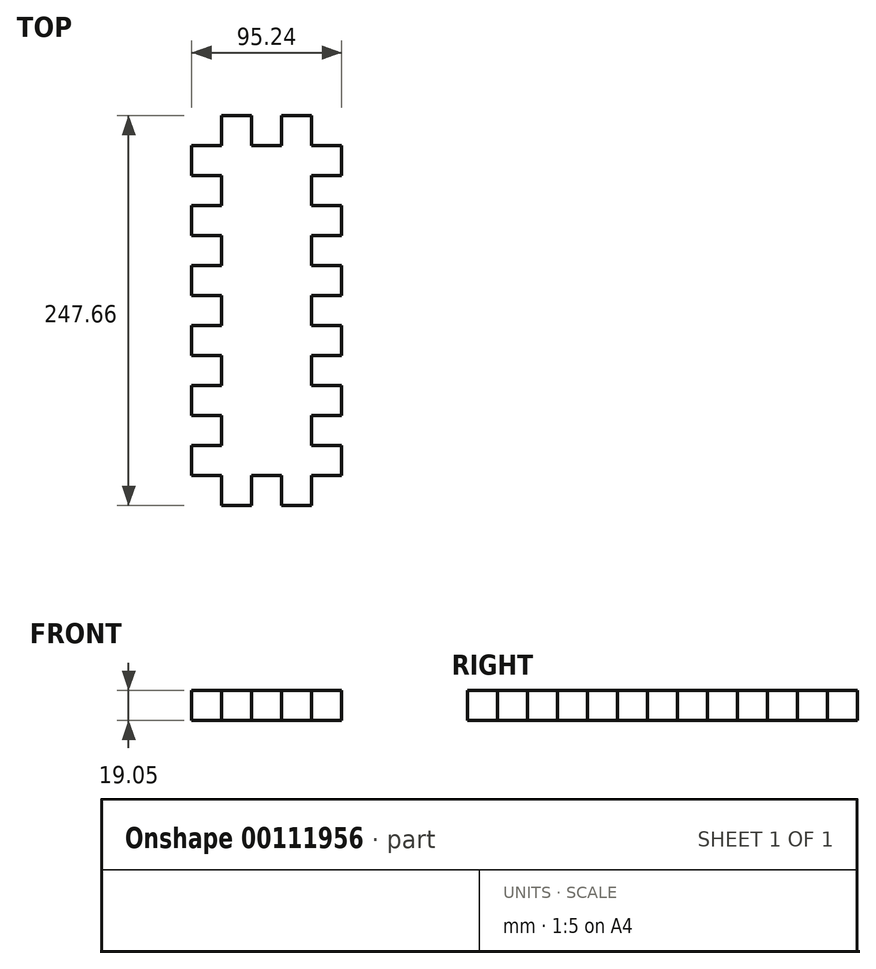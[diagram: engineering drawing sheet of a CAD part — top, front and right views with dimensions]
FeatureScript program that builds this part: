
annotation { "Feature Type Name" : "Feature", "Feature Type Description" : "" }
export const myFeature = defineFeature(function(context is Context, id is Id, definition is map)
    precondition{}
    {
        {
            var Q0;
            Q0=qCreatedBy(makeId("Top.planeOp"),FACE);
            var sketch = newSketch(context, id + "F0", { "sketchPlane" : qUnion([Q0])});
            skLineSegment(sketch, "E0.bottom", {"start": v(-47.62, 123.83) * mm, "end": v(47.63, 123.83) * mm});
            skLineSegment(sketch, "E0.top", {"start": v(-47.63, -123.83) * mm, "end": v(47.62, -123.83) * mm});
            skLineSegment(sketch, "E0.left", {"start": v(-47.62, 123.83) * mm, "end": v(-47.63, -123.83) * mm});
            skLineSegment(sketch, "E0.right", {"start": v(47.63, 123.83) * mm, "end": v(47.62, -123.83) * mm});
            skPoint(sketch, "E0.middle", {"position": v(0, 0) * mm});
            skSolve(sketch);
        }
        {
            var Q0;
            Q0 = qSketchRegion(id + "F0", true);
            extrude(context, id + "F1", {"entities" : qUnion([Q0]), "depth" : 19.05 * mm});
        }
        {
            var Q0;
            Q0=makeQuery(id+"F1.opExtrude","CAP_FACE",FACE,{"disambiguationData":[OSD([sQuery(id+"F0.wireOp",EDGE,"E0.bottom"),sQuery(id+"F0.wireOp",EDGE,"E0.top"),sQuery(id+"F0.wireOp",EDGE,"E0.left"),sQuery(id+"F0.wireOp",EDGE,"E0.right")])],"isStart":false});
            var sketch = newSketch(context, id + "F2", { "sketchPlane" : qUnion([Q0])});
            skLineSegment(sketch, "E1.bottom", {"start": v(-47.62, 123.83) * mm, "end": v(-28.57, 123.83) * mm});
            skLineSegment(sketch, "E1.top", {"start": v(-47.62, 104.78) * mm, "end": v(-28.57, 104.78) * mm});
            skLineSegment(sketch, "E1.left", {"start": v(-47.62, 123.83) * mm, "end": v(-47.62, 104.78) * mm});
            skLineSegment(sketch, "E1.right", {"start": v(-28.57, 123.83) * mm, "end": v(-28.57, 104.78) * mm});
            skLineSegment(sketch, "E2.1.0.0", {"start": v(9.53, 123.83) * mm, "end": v(9.53, 104.78) * mm});
            skLineSegment(sketch, "E2.1.0.1", {"start": v(-9.52, 123.83) * mm, "end": v(-9.52, 104.78) * mm});
            skLineSegment(sketch, "E2.1.0.2", {"start": v(-9.52, 104.78) * mm, "end": v(9.53, 104.78) * mm});
            skLineSegment(sketch, "E2.1.0.3", {"start": v(-9.52, 123.83) * mm, "end": v(9.53, 123.83) * mm});
            skLineSegment(sketch, "E2.2.0.0", {"start": v(47.63, 123.83) * mm, "end": v(47.63, 104.78) * mm});
            skLineSegment(sketch, "E2.2.0.1", {"start": v(28.58, 123.83) * mm, "end": v(28.58, 104.78) * mm});
            skLineSegment(sketch, "E2.2.0.2", {"start": v(28.58, 104.78) * mm, "end": v(47.63, 104.78) * mm});
            skLineSegment(sketch, "E2.2.0.3", {"start": v(28.58, 123.83) * mm, "end": v(47.63, 123.83) * mm});
            skLineSegment(sketch, "E2.direction1", {"start": v(-47.62, 104.78) * mm, "end": v(-9.52, 104.78) * mm, "construction": true});
            skLineSegment(sketch, "E3.0.1.0", {"start": v(-47.62, 85.73) * mm, "end": v(-28.57, 85.73) * mm});
            skLineSegment(sketch, "E3.0.1.1", {"start": v(-47.62, 66.68) * mm, "end": v(-28.57, 66.68) * mm});
            skLineSegment(sketch, "E3.0.1.2", {"start": v(-47.62, 85.73) * mm, "end": v(-47.62, 66.68) * mm});
            skLineSegment(sketch, "E3.0.1.3", {"start": v(-28.57, 85.73) * mm, "end": v(-28.57, 66.68) * mm});
            skLineSegment(sketch, "E3.0.2.0", {"start": v(-47.62, 47.63) * mm, "end": v(-28.57, 47.63) * mm});
            skLineSegment(sketch, "E3.0.2.1", {"start": v(-47.62, 28.58) * mm, "end": v(-28.57, 28.58) * mm});
            skLineSegment(sketch, "E3.0.2.2", {"start": v(-47.62, 47.63) * mm, "end": v(-47.62, 28.58) * mm});
            skLineSegment(sketch, "E3.0.2.3", {"start": v(-28.57, 47.63) * mm, "end": v(-28.57, 28.58) * mm});
            skLineSegment(sketch, "E3.0.3.0", {"start": v(-47.62, 9.53) * mm, "end": v(-28.57, 9.53) * mm});
            skLineSegment(sketch, "E3.0.3.1", {"start": v(-47.62, -9.52) * mm, "end": v(-28.57, -9.52) * mm});
            skLineSegment(sketch, "E3.0.3.2", {"start": v(-47.62, 9.53) * mm, "end": v(-47.62, -9.52) * mm});
            skLineSegment(sketch, "E3.0.3.3", {"start": v(-28.57, 9.53) * mm, "end": v(-28.57, -9.52) * mm});
            skLineSegment(sketch, "E3.0.4.0", {"start": v(-47.62, -28.57) * mm, "end": v(-28.57, -28.57) * mm});
            skLineSegment(sketch, "E3.0.4.1", {"start": v(-47.62, -47.62) * mm, "end": v(-28.57, -47.62) * mm});
            skLineSegment(sketch, "E3.0.4.2", {"start": v(-47.62, -28.57) * mm, "end": v(-47.62, -47.62) * mm});
            skLineSegment(sketch, "E3.0.4.3", {"start": v(-28.57, -28.57) * mm, "end": v(-28.57, -47.62) * mm});
            skLineSegment(sketch, "E3.0.5.0", {"start": v(-47.62, -66.67) * mm, "end": v(-28.57, -66.67) * mm});
            skLineSegment(sketch, "E3.0.5.1", {"start": v(-47.62, -85.72) * mm, "end": v(-28.57, -85.72) * mm});
            skLineSegment(sketch, "E3.0.5.2", {"start": v(-47.62, -66.67) * mm, "end": v(-47.62, -85.72) * mm});
            skLineSegment(sketch, "E3.0.5.3", {"start": v(-28.57, -66.67) * mm, "end": v(-28.57, -85.72) * mm});
            skLineSegment(sketch, "E3.direction1", {"start": v(-47.62, 104.78) * mm, "end": v(-22.22, 104.78) * mm, "construction": true});
            skLineSegment(sketch, "E3.direction2", {"start": v(-47.62, 104.78) * mm, "end": v(-47.62, 66.68) * mm, "construction": true});
            skLineSegment(sketch, "E4.0.0.6", {"start": v(-47.62, -104.77) * mm, "end": v(-28.57, -104.77) * mm});
            skLineSegment(sketch, "E4.3.0.6", {"start": v(-47.62, -123.82) * mm, "end": v(-28.57, -123.82) * mm});
            skLineSegment(sketch, "E4.6.0.6", {"start": v(-47.62, -104.77) * mm, "end": v(-47.62, -123.82) * mm});
            skLineSegment(sketch, "E4.9.0.6", {"start": v(-28.57, -104.77) * mm, "end": v(-28.57, -123.82) * mm});
            skLineSegment(sketch, "E5.1.0.0", {"start": v(-9.52, -104.77) * mm, "end": v(9.53, -104.77) * mm});
            skLineSegment(sketch, "E5.1.0.1", {"start": v(-9.52, -123.82) * mm, "end": v(9.53, -123.82) * mm});
            skLineSegment(sketch, "E5.1.0.2", {"start": v(-9.52, -104.77) * mm, "end": v(-9.52, -123.82) * mm});
            skLineSegment(sketch, "E5.1.0.3", {"start": v(9.53, -104.77) * mm, "end": v(9.53, -123.82) * mm});
            skLineSegment(sketch, "E5.2.0.0", {"start": v(28.58, -104.77) * mm, "end": v(47.63, -104.77) * mm});
            skLineSegment(sketch, "E5.2.0.1", {"start": v(28.58, -123.82) * mm, "end": v(47.63, -123.82) * mm});
            skLineSegment(sketch, "E5.2.0.2", {"start": v(28.58, -104.77) * mm, "end": v(28.58, -123.82) * mm});
            skLineSegment(sketch, "E5.2.0.3", {"start": v(47.63, -104.77) * mm, "end": v(47.63, -123.82) * mm});
            skLineSegment(sketch, "E5.direction1", {"start": v(-47.62, -123.82) * mm, "end": v(-9.52, -123.82) * mm, "construction": true});
            skLineSegment(sketch, "E6.0.1.0", {"start": v(28.58, -66.67) * mm, "end": v(47.63, -66.67) * mm});
            skLineSegment(sketch, "E6.0.1.1", {"start": v(28.58, -66.67) * mm, "end": v(28.58, -85.72) * mm});
            skLineSegment(sketch, "E6.0.1.2", {"start": v(47.63, -66.67) * mm, "end": v(47.63, -85.72) * mm});
            skLineSegment(sketch, "E6.0.1.3", {"start": v(28.58, -85.72) * mm, "end": v(47.63, -85.72) * mm});
            skLineSegment(sketch, "E6.0.2.0", {"start": v(28.58, -28.57) * mm, "end": v(47.63, -28.57) * mm});
            skLineSegment(sketch, "E6.0.2.1", {"start": v(28.58, -28.57) * mm, "end": v(28.58, -47.62) * mm});
            skLineSegment(sketch, "E6.0.2.2", {"start": v(47.63, -28.57) * mm, "end": v(47.63, -47.62) * mm});
            skLineSegment(sketch, "E6.0.2.3", {"start": v(28.58, -47.62) * mm, "end": v(47.63, -47.62) * mm});
            skLineSegment(sketch, "E6.0.3.0", {"start": v(28.58, 9.53) * mm, "end": v(47.63, 9.53) * mm});
            skLineSegment(sketch, "E6.0.3.1", {"start": v(28.58, 9.53) * mm, "end": v(28.58, -9.52) * mm});
            skLineSegment(sketch, "E6.0.3.2", {"start": v(47.63, 9.53) * mm, "end": v(47.63, -9.52) * mm});
            skLineSegment(sketch, "E6.0.3.3", {"start": v(28.58, -9.52) * mm, "end": v(47.63, -9.52) * mm});
            skLineSegment(sketch, "E6.0.4.0", {"start": v(28.58, 47.63) * mm, "end": v(47.63, 47.63) * mm});
            skLineSegment(sketch, "E6.0.4.1", {"start": v(28.58, 47.63) * mm, "end": v(28.58, 28.58) * mm});
            skLineSegment(sketch, "E6.0.4.2", {"start": v(47.63, 47.63) * mm, "end": v(47.63, 28.58) * mm});
            skLineSegment(sketch, "E6.0.4.3", {"start": v(28.58, 28.58) * mm, "end": v(47.63, 28.58) * mm});
            skLineSegment(sketch, "E6.0.5.0", {"start": v(28.58, 85.73) * mm, "end": v(47.63, 85.73) * mm});
            skLineSegment(sketch, "E6.0.5.1", {"start": v(28.58, 85.73) * mm, "end": v(28.58, 66.68) * mm});
            skLineSegment(sketch, "E6.0.5.2", {"start": v(47.63, 85.73) * mm, "end": v(47.63, 66.68) * mm});
            skLineSegment(sketch, "E6.0.5.3", {"start": v(28.58, 66.68) * mm, "end": v(47.63, 66.68) * mm});
            skLineSegment(sketch, "E6.direction1", {"start": v(28.58, -123.82) * mm, "end": v(53.98, -123.82) * mm, "construction": true});
            skLineSegment(sketch, "E6.direction2", {"start": v(28.58, -123.82) * mm, "end": v(28.58, -85.72) * mm, "construction": true});
            skSolve(sketch);
        }
        {
            var Q0;
            {var subQ25=sQuery(id+"F2.wireOp",EDGE,"E1.top");Q0=makeQuery(id+"F2.imprint","IMPRINT",FACE,{"disambiguationData":[TD([[makeQuery(id+"F2.imprint","IMPRINT",EDGE,{"derivedFrom":subQ25}),-1.0]])]});}
            extrude(context, id + "F3", {"entities" : qUnion([Q0]), "operationType" : NewBodyOperationType.INTERSECT, "endBound" : BoundingType.THROUGH_ALL, "oppositeDirection" : true, "depth" : 25.4 * mm});
        }
    });
